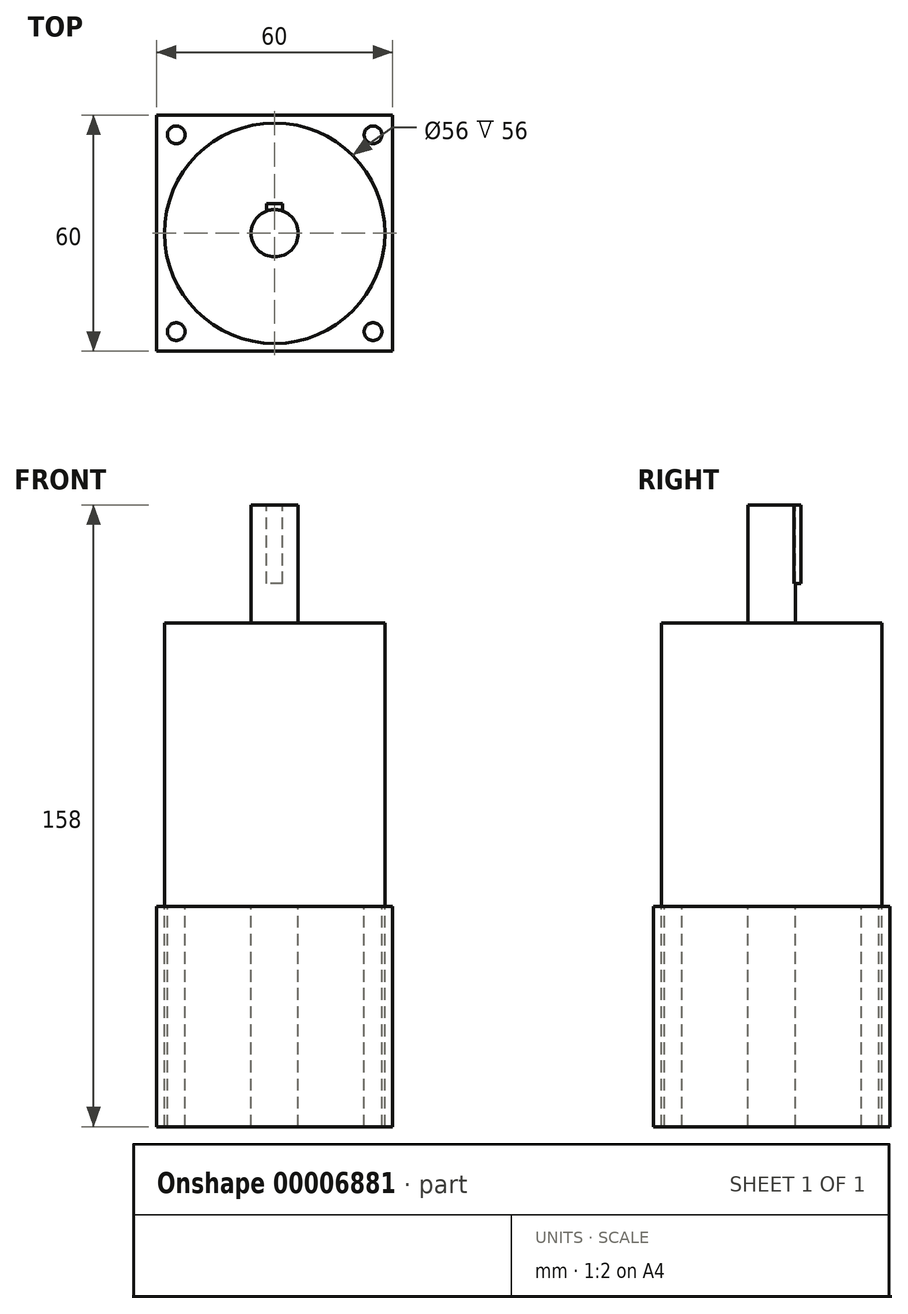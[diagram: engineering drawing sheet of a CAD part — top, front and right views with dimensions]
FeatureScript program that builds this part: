
annotation { "Feature Type Name" : "Feature", "Feature Type Description" : "" }
export const myFeature = defineFeature(function(context is Context, id is Id, definition is map)
    precondition{}
    {
        {
            var Q0;
            Q0=qCreatedBy(makeId("Top.planeOp"),FACE);
            var sketch = newSketch(context, id + "F0", { "sketchPlane" : qUnion([Q0])});
            skLineSegment(sketch, "E0.rect.bottom", {"start": v(30, -30) * mm, "end": v(-30, -30) * mm});
            skLineSegment(sketch, "E0.rect.top", {"start": v(30, 30) * mm, "end": v(-30, 30) * mm});
            skLineSegment(sketch, "E0.rect.left", {"start": v(30, -30) * mm, "end": v(30, 30) * mm});
            skLineSegment(sketch, "E0.rect.right", {"start": v(-30, -30) * mm, "end": v(-30, 30) * mm});
            skPoint(sketch, "E0.rect.middle", {"position": v(0, 0) * mm});
            skSolve(sketch);
        }
        {
            var Q0;
            Q0=qSketchRegion(id+"F0",true);
            extrude(context, id + "F1", {"entities" : qUnion([Q0]), "depth" : (56) * mm});
        }
        {
            var Q0;
            Q0=makeQuery(id+"F1.opExtrude","CAP_FACE",FACE,{"disambiguationData":[OSD([sQuery(id+"F0.wireOp",EDGE,"E0.rect.bottom"),sQuery(id+"F0.wireOp",EDGE,"E0.rect.top"),sQuery(id+"F0.wireOp",EDGE,"E0.rect.left"),sQuery(id+"F0.wireOp",EDGE,"E0.rect.right")])],"isStart":false});
            var sketch = newSketch(context, id + "F2", { "sketchPlane" : qUnion([Q0])});
            skCircle(sketch, "E1", {"center": v(0, 0) * mm, "radius": 28 * mm});
            skCircle(sketch, "E2", {"center": v(-25, 25) * mm, "radius": 2.25 * mm});
            skCircle(sketch, "E3", {"center": v(25, 25) * mm, "radius": 2.25 * mm});
            skCircle(sketch, "E4", {"center": v(25, -25) * mm, "radius": 2.25 * mm});
            skCircle(sketch, "E5", {"center": v(-25, -25) * mm, "radius": 2.25 * mm});
            skCircle(sketch, "E6", {"center": v(0, 0) * mm, "radius": 6 * mm});
            skLineSegment(sketch, "E7", {"start": v(-30, 0) * mm, "end": v(30, 0) * mm, "construction": true});
            skLineSegment(sketch, "E8", {"start": v(0, 30) * mm, "end": v(0, -30) * mm, "construction": true});
            skSolve(sketch);
        }
        {
            var Q0;
            Q0=makeQuery(id+"F2.imprint","IMPRINT",FACE,{"disambiguationData":[TD([[makeQuery(id+"F2.imprint","IMPRINT",EDGE,{"derivedFrom":sQuery(id+"F2.wireOp",EDGE,"E6")}),1.0]])]});
            extrude(context, id + "F3", {"entities" : qUnion([Q0]), "operationType" : NewBodyOperationType.ADD, "depth" : (102) * mm});
        }
        {
            var Q0;
            Q0=makeQuery(id+"F2.imprint","IMPRINT",FACE,{"disambiguationData":[TD([[makeQuery(id+"F2.imprint","IMPRINT",EDGE,{"derivedFrom":sQuery(id+"F2.wireOp",EDGE,"E1")}),1.0]])]});
            extrude(context, id + "F4", {"entities" : qUnion([Q0]), "operationType" : NewBodyOperationType.ADD, "depth" : (72) * mm});
        }
        {
            var Q0;
            Q0=makeQuery(id+"F2.imprint","IMPRINT",FACE,{"disambiguationData":[TD([[makeQuery(id+"F2.imprint","IMPRINT",EDGE,{"derivedFrom":sQuery(id+"F2.wireOp",EDGE,"E3")}),1.0]])]});
            var Q1;
            Q1=makeQuery(id+"F2.imprint","IMPRINT",FACE,{"disambiguationData":[TD([[makeQuery(id+"F2.imprint","IMPRINT",EDGE,{"derivedFrom":sQuery(id+"F2.wireOp",EDGE,"E4")}),1.0]])]});
            var Q2;
            Q2=makeQuery(id+"F2.imprint","IMPRINT",FACE,{"disambiguationData":[TD([[makeQuery(id+"F2.imprint","IMPRINT",EDGE,{"derivedFrom":sQuery(id+"F2.wireOp",EDGE,"E1")}),1.0]])]});
            var Q3;
            Q3=makeQuery(id+"F2.imprint","IMPRINT",FACE,{"disambiguationData":[TD([[makeQuery(id+"F2.imprint","IMPRINT",EDGE,{"derivedFrom":sQuery(id+"F2.wireOp",EDGE,"E2")}),1.0]])]});
            var Q4;
            Q4=makeQuery(id+"F2.imprint","IMPRINT",FACE,{"disambiguationData":[TD([[makeQuery(id+"F2.imprint","IMPRINT",EDGE,{"derivedFrom":sQuery(id+"F2.wireOp",EDGE,"E5")}),1.0]])]});
            extrude(context, id + "F5", {"entities" : qUnion([Q0, Q1, Q2, Q3, Q4]), "operationType" : NewBodyOperationType.REMOVE, "endBound" : BoundingType.THROUGH_ALL, "oppositeDirection" : true, "depth" : 25 * mm});
        }
        {
            var Q0;
            Q0=makeQuery(id+"F3.opExtrude","CAP_FACE",FACE,{"disambiguationData":[OSD([sQuery(id+"F2.wireOp",EDGE,"E6")])],"isStart":false});
            var sketch = newSketch(context, id + "F6", { "sketchPlane" : qUnion([Q0])});
            skLineSegment(sketch, "E9", {"start": v(0, 0) * mm, "end": v(0, 6) * mm, "construction": true});
            skLineSegment(sketch, "E10", {"start": v(0, 6) * mm, "end": v(0, -6) * mm, "construction": true});
            skLineSegment(sketch, "E11", {"start": v(-6, 0) * mm, "end": v(6, 0) * mm, "construction": true});
            skLineSegment(sketch, "E12.rect.top", {"start": v(2, 7.47) * mm, "end": v(-2, 7.47) * mm});
            skLineSegment(sketch, "E12.rect.left", {"start": v(2, 5.66) * mm, "end": v(2, 7.47) * mm});
            skLineSegment(sketch, "E12.rect.right", {"start": v(-2, 5.66) * mm, "end": v(-2, 7.47) * mm});
            skPoint(sketch, "E12.rect.middle", {"position": v(0, 6) * mm});
            skCircle(sketch, "E13", {"center": v(0, 0) * mm, "radius": 6 * mm});
            skPoint(sketch, "E14.orphan", {"position": v(2, 4.53) * mm});
            skPoint(sketch, "E15.orphan", {"position": v(-2, 4.53) * mm});
            skSolve(sketch);
        }
        {
            var Q0;
            Q0=makeQuery(id+"F6.imprint","IMPRINT",FACE,{"disambiguationData":[TD([[makeQuery(id+"F6.imprint","IMPRINT",EDGE,{"derivedFrom":sQuery(id+"F6.wireOp",EDGE,"E12.rect.top")}),1.0]])]});
            extrude(context, id + "F7", {"entities" : qUnion([Q0]), "oppositeDirection" : true, "depth" : (20) * mm});
        }
        {
            var Q0;
            Q0=makeQuery(id+"F5.boolean.opBoolean","COPY",FACE,{"derivedFrom":makeQuery(id+"F5.opExtrude","CAP_FACE",FACE,{"disambiguationData":[OSD([sQuery(id+"F2.wireOp",EDGE,"E1"),sQuery(id+"F2.wireOp",EDGE,"E6")])],"isStart":true})});
            extrude(context, id + "F8", {"entities" : qUnion([Q0]), "depth" : (150) * mm});
        }
        {
            var Q0;
            Q0=makeQuery(id+"F8.opExtrude","CAP_FACE",FACE,{"disambiguationData":[OSD([sQuery(id+"F2.wireOp",EDGE,"E1"),sQuery(id+"F2.wireOp",EDGE,"E6")])],"isStart":false});
            extrude(context, id + "F9", {"entities" : qUnion([Q0]), "operationType" : NewBodyOperationType.REMOVE, "oppositeDirection" : true, "depth" : (94) * mm});
        }
    });
